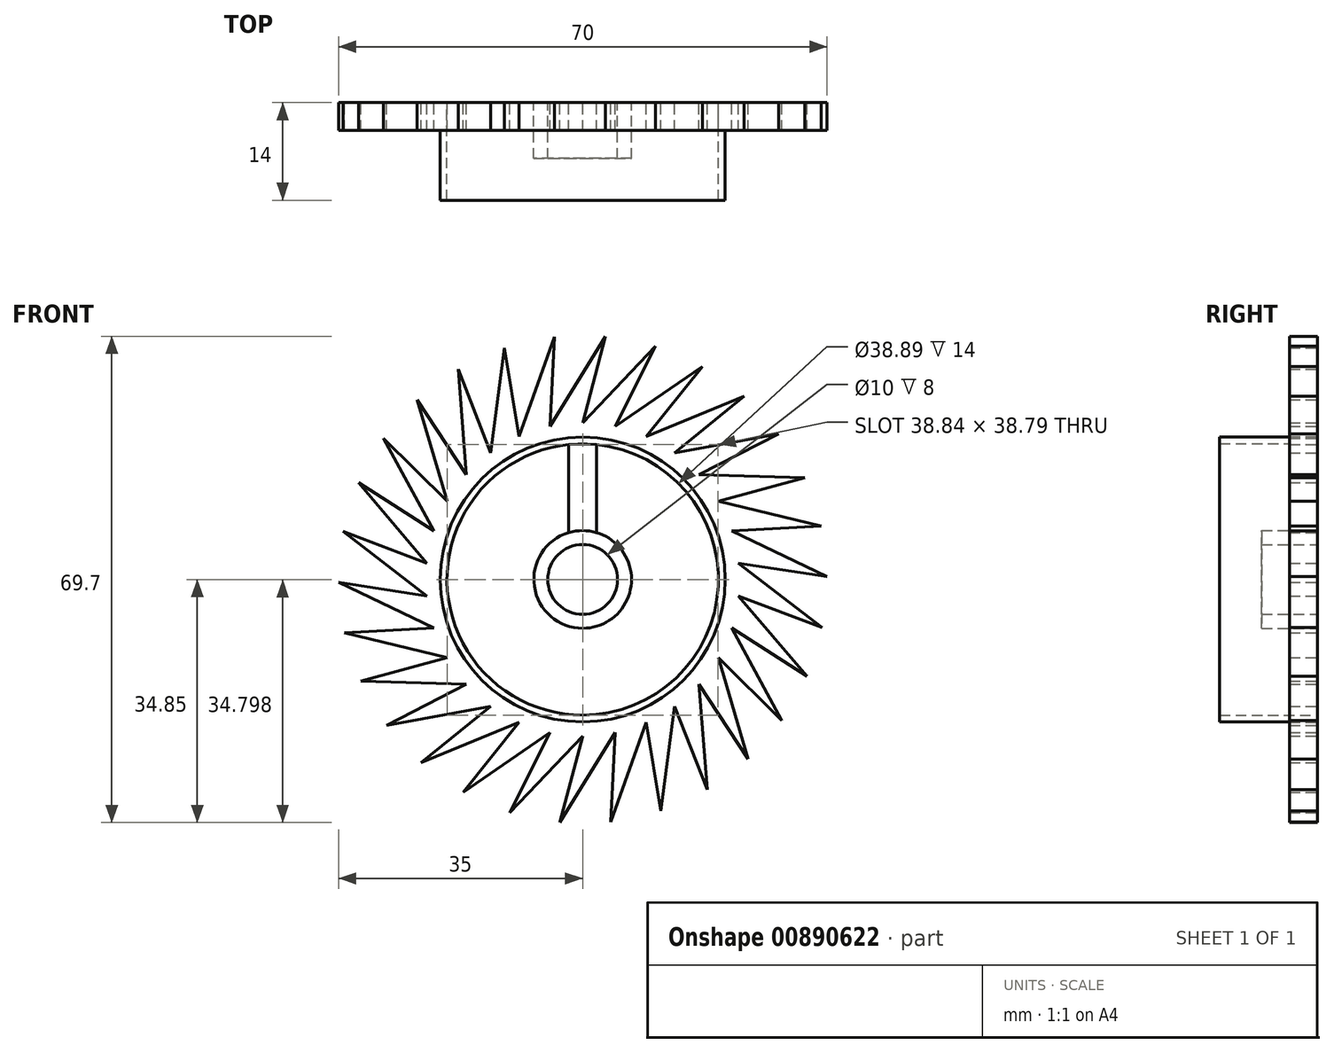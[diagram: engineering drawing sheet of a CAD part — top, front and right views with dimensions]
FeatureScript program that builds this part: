
annotation { "Feature Type Name" : "Feature", "Feature Type Description" : "" }
export const myFeature = defineFeature(function(context is Context, id is Id, definition is map)
    precondition{}
    {
        {
            var Q0;
            Q0=qCreatedBy(makeId("Front.planeOp"),FACE);
            var sketch = newSketch(context, id + "F0", { "sketchPlane" : qUnion([Q0])});
            skLineSegment(sketch, "E0", {"start": v(0, 0) * mm, "end": v(0, 22.44) * mm, "construction": true});
            skLineSegment(sketch, "E1", {"start": v(0, 0) * mm, "end": v(4.67, 21.95) * mm, "construction": true});
            skCircle(sketch, "E2", {"center": v(0, 0) * mm, "radius": 22.44 * mm, "construction": true});
            skLineSegment(sketch, "E3", {"start": v(0, 22.44) * mm, "end": v(10.44, 33.4) * mm});
            skLineSegment(sketch, "E4", {"start": v(10.44, 33.4) * mm, "end": v(4.67, 21.95) * mm});
            skCircle(sketch, "E5", {"center": v(0, 0) * mm, "radius": 35 * mm, "construction": true});
            skCircle(sketch, "E6", {"center": v(0, 0) * mm, "radius": 19.44 * mm});
            skLineSegment(sketch, "E7.1.0", {"start": v(-4.67, 21.95) * mm, "end": v(3.27, 34.85) * mm});
            skLineSegment(sketch, "E7.1.1", {"start": v(3.27, 34.85) * mm, "end": v(0, 22.44) * mm});
            skLineSegment(sketch, "E7.2.0", {"start": v(-9.13, 20.5) * mm, "end": v(-4.05, 34.76) * mm});
            skLineSegment(sketch, "E7.2.1", {"start": v(-4.05, 34.76) * mm, "end": v(-4.67, 21.95) * mm});
            skLineSegment(sketch, "E7.3.0", {"start": v(-13.2, 18.16) * mm, "end": v(-11.2, 33.16) * mm});
            skLineSegment(sketch, "E7.3.1", {"start": v(-11.2, 33.16) * mm, "end": v(-9.13, 20.5) * mm});
            skLineSegment(sketch, "E7.4.0", {"start": v(-16.68, 15.02) * mm, "end": v(-17.84, 30.11) * mm});
            skLineSegment(sketch, "E7.4.1", {"start": v(-17.84, 30.11) * mm, "end": v(-13.2, 18.16) * mm});
            skLineSegment(sketch, "E7.5.0", {"start": v(-19.44, 11.22) * mm, "end": v(-23.71, 25.74) * mm});
            skLineSegment(sketch, "E7.5.1", {"start": v(-23.71, 25.74) * mm, "end": v(-16.68, 15.02) * mm});
            skLineSegment(sketch, "E7.6.0", {"start": v(-21.35, 6.94) * mm, "end": v(-28.55, 20.25) * mm});
            skLineSegment(sketch, "E7.6.1", {"start": v(-28.55, 20.25) * mm, "end": v(-19.44, 11.22) * mm});
            skLineSegment(sketch, "E7.7.0", {"start": v(-22.32, 2.35) * mm, "end": v(-32.13, 13.87) * mm});
            skLineSegment(sketch, "E7.7.1", {"start": v(-32.13, 13.87) * mm, "end": v(-21.35, 6.94) * mm});
            skLineSegment(sketch, "E7.8.0", {"start": v(-22.32, -2.35) * mm, "end": v(-34.32, 6.89) * mm});
            skLineSegment(sketch, "E7.8.1", {"start": v(-34.32, 6.89) * mm, "end": v(-22.32, 2.35) * mm});
            skLineSegment(sketch, "E7.9.0", {"start": v(-21.35, -6.94) * mm, "end": v(-35, -0.4) * mm});
            skLineSegment(sketch, "E7.9.1", {"start": v(-35, -0.4) * mm, "end": v(-22.32, -2.35) * mm});
            skLineSegment(sketch, "E7.10.0", {"start": v(-19.44, -11.22) * mm, "end": v(-34.15, -7.66) * mm});
            skLineSegment(sketch, "E7.10.1", {"start": v(-34.15, -7.66) * mm, "end": v(-21.35, -6.94) * mm});
            skLineSegment(sketch, "E7.11.0", {"start": v(-16.68, -15.02) * mm, "end": v(-31.81, -14.6) * mm});
            skLineSegment(sketch, "E7.11.1", {"start": v(-31.81, -14.6) * mm, "end": v(-19.44, -11.22) * mm});
            skLineSegment(sketch, "E7.12.0", {"start": v(-13.2, -18.16) * mm, "end": v(-28.08, -20.9) * mm});
            skLineSegment(sketch, "E7.12.1", {"start": v(-28.08, -20.9) * mm, "end": v(-16.68, -15.02) * mm});
            skLineSegment(sketch, "E7.13.0", {"start": v(-9.13, -20.5) * mm, "end": v(-23.12, -26.27) * mm});
            skLineSegment(sketch, "E7.13.1", {"start": v(-23.12, -26.27) * mm, "end": v(-13.2, -18.16) * mm});
            skLineSegment(sketch, "E7.14.0", {"start": v(-4.67, -21.95) * mm, "end": v(-17.16, -30.5) * mm});
            skLineSegment(sketch, "E7.14.1", {"start": v(-17.16, -30.5) * mm, "end": v(-9.13, -20.5) * mm});
            skLineSegment(sketch, "E7.15.0", {"start": v(0, -22.44) * mm, "end": v(-10.44, -33.4) * mm});
            skLineSegment(sketch, "E7.15.1", {"start": v(-10.44, -33.4) * mm, "end": v(-4.67, -21.95) * mm});
            skLineSegment(sketch, "E7.16.0", {"start": v(4.67, -21.95) * mm, "end": v(-3.27, -34.85) * mm});
            skLineSegment(sketch, "E7.16.1", {"start": v(-3.27, -34.85) * mm, "end": v(0, -22.44) * mm});
            skLineSegment(sketch, "E7.17.0", {"start": v(9.13, -20.5) * mm, "end": v(4.05, -34.76) * mm});
            skLineSegment(sketch, "E7.17.1", {"start": v(4.05, -34.76) * mm, "end": v(4.67, -21.95) * mm});
            skLineSegment(sketch, "E7.18.0", {"start": v(13.2, -18.16) * mm, "end": v(11.2, -33.16) * mm});
            skLineSegment(sketch, "E7.18.1", {"start": v(11.2, -33.16) * mm, "end": v(9.13, -20.5) * mm});
            skLineSegment(sketch, "E7.19.0", {"start": v(16.68, -15.02) * mm, "end": v(17.84, -30.11) * mm});
            skLineSegment(sketch, "E7.19.1", {"start": v(17.84, -30.11) * mm, "end": v(13.2, -18.16) * mm});
            skLineSegment(sketch, "E7.20.0", {"start": v(19.44, -11.22) * mm, "end": v(23.71, -25.74) * mm});
            skLineSegment(sketch, "E7.20.1", {"start": v(23.71, -25.74) * mm, "end": v(16.68, -15.02) * mm});
            skLineSegment(sketch, "E7.21.0", {"start": v(21.35, -6.94) * mm, "end": v(28.55, -20.25) * mm});
            skLineSegment(sketch, "E7.21.1", {"start": v(28.55, -20.25) * mm, "end": v(19.44, -11.22) * mm});
            skLineSegment(sketch, "E7.22.0", {"start": v(22.32, -2.35) * mm, "end": v(32.13, -13.87) * mm});
            skLineSegment(sketch, "E7.22.1", {"start": v(32.13, -13.87) * mm, "end": v(21.35, -6.94) * mm});
            skLineSegment(sketch, "E7.23.0", {"start": v(22.32, 2.35) * mm, "end": v(34.32, -6.89) * mm});
            skLineSegment(sketch, "E7.23.1", {"start": v(34.32, -6.89) * mm, "end": v(22.32, -2.35) * mm});
            skLineSegment(sketch, "E7.24.0", {"start": v(21.35, 6.94) * mm, "end": v(35, 0.4) * mm});
            skLineSegment(sketch, "E7.24.1", {"start": v(35, 0.4) * mm, "end": v(22.32, 2.35) * mm});
            skLineSegment(sketch, "E7.25.0", {"start": v(19.44, 11.22) * mm, "end": v(34.15, 7.66) * mm});
            skLineSegment(sketch, "E7.25.1", {"start": v(34.15, 7.66) * mm, "end": v(21.35, 6.94) * mm});
            skLineSegment(sketch, "E7.26.0", {"start": v(16.68, 15.02) * mm, "end": v(31.81, 14.6) * mm});
            skLineSegment(sketch, "E7.26.1", {"start": v(31.81, 14.6) * mm, "end": v(19.44, 11.22) * mm});
            skLineSegment(sketch, "E7.27.0", {"start": v(13.2, 18.16) * mm, "end": v(28.08, 20.9) * mm});
            skLineSegment(sketch, "E7.27.1", {"start": v(28.08, 20.9) * mm, "end": v(16.68, 15.02) * mm});
            skLineSegment(sketch, "E7.28.0", {"start": v(9.13, 20.5) * mm, "end": v(23.12, 26.27) * mm});
            skLineSegment(sketch, "E7.28.1", {"start": v(23.12, 26.27) * mm, "end": v(13.2, 18.16) * mm});
            skLineSegment(sketch, "E7.29.0", {"start": v(4.67, 21.95) * mm, "end": v(17.16, 30.5) * mm});
            skLineSegment(sketch, "E7.29.1", {"start": v(17.16, 30.5) * mm, "end": v(9.13, 20.5) * mm});
            skCircle(sketch, "E8", {"center": v(0, 0) * mm, "radius": 1.5 * mm});
            skCircle(sketch, "E9", {"center": v(0, 0) * mm, "radius": 5 * mm});
            skLineSegment(sketch, "E10.top", {"start": v(-2, 22.36) * mm, "end": v(2, 22.36) * mm});
            skLineSegment(sketch, "E10.left", {"start": v(-2, 6.7) * mm, "end": v(-2, 22.36) * mm});
            skLineSegment(sketch, "E10.right", {"start": v(2, 6.7) * mm, "end": v(2, 22.36) * mm});
            skPoint(sketch, "E10.middle", {"position": v(0, 14.53) * mm});
            skCircle(sketch, "E11", {"center": v(0, 0) * mm, "radius": 7 * mm});
            skCircle(sketch, "E12", {"center": v(0, 0) * mm, "radius": 20.41 * mm});
            skSolve(sketch);
        }
        {
            var Q0;
            Q0=qCreatedBy(makeId("Top.planeOp"),FACE);
            var sketch = newSketch(context, id + "F1", { "sketchPlane" : qUnion([Q0])});
            skLineSegment(sketch, "E13", {"start": v(0, 0) * mm, "end": v(0, -18.3) * mm, "construction": true});
            skSolve(sketch);
        }
        {
            var Q0;
            Q0=makeQuery(id+"F0.imprint","IMPRINT",FACE,{"disambiguationData":[TD([[makeQuery(id+"F0.imprint","IMPRINT",EDGE,{"derivedFrom":sQuery(id+"F0.wireOp",EDGE,"E3")}),-1.0]])]});
            var Q1;
            {var subQ0=sQuery(id+"F0.wireOp",EDGE,"E10.top");Q1=makeQuery(id+"F0.imprint","IMPRINT",FACE,{"disambiguationData":[TD([[makeQuery(id+"F0.imprint","IMPRINT",EDGE,{"derivedFrom":subQ0}),-1.0]])]});}
            var Q2;
            {var subQ0=sQuery(id+"F0.wireOp",EDGE,"E10.left");var subQ1=sQuery(id+"F0.wireOp",EDGE,"E6");var subQ2=makeQuery(id+"F0.imprint","INTERSECT",VERTEX,{"derivedFrom":[subQ1,subQ0]});Q2=makeQuery(id+"F0.imprint","IMPRINT",FACE,{"disambiguationData":[TD([[makeQuery(id+"F0.imprint","IMPRINT",EDGE,{"disambiguationData":[TD([[subQ2,-1.0]])],"derivedFrom":subQ1}),-1.0]])]});}
            extrude(context, id + "F2", {"entities" : qUnion([Q0, Q1, Q2]), "depth" : 4 * mm, "offsetDistance" : 25 * mm});
        }
        {
            var Q0;
            {var subQ0=sQuery(id+"F0.wireOp",EDGE,"E10.left");var subQ1=sQuery(id+"F0.wireOp",EDGE,"E6");var subQ2=makeQuery(id+"F0.imprint","INTERSECT",VERTEX,{"derivedFrom":[subQ1,subQ0]});Q0=makeQuery(id+"F0.imprint","IMPRINT",FACE,{"disambiguationData":[TD([[makeQuery(id+"F0.imprint","IMPRINT",EDGE,{"disambiguationData":[TD([[subQ2,-1.0]])],"derivedFrom":subQ1}),-1.0]])]});}
            var Q1;
            {var subQ0=sQuery(id+"F0.wireOp",EDGE,"E10.left");var subQ1=sQuery(id+"F0.wireOp",EDGE,"E6");var subQ2=makeQuery(id+"F0.imprint","INTERSECT",VERTEX,{"derivedFrom":[subQ1,subQ0]});Q1=makeQuery(id+"F0.imprint","IMPRINT",FACE,{"disambiguationData":[TD([[makeQuery(id+"F0.imprint","IMPRINT",EDGE,{"disambiguationData":[TD([[subQ2,1.0]])],"derivedFrom":subQ1}),-1.0]])]});}
            extrude(context, id + "F3", {"entities" : qUnion([Q0, Q1]), "operationType" : NewBodyOperationType.ADD, "depth" : 14 * mm, "offsetDistance" : 25 * mm});
        }
        {
            var Q0;
            Q0=makeQuery(id+"F0.imprint","IMPRINT",FACE,{"disambiguationData":[TD([[makeQuery(id+"F0.imprint","IMPRINT",EDGE,{"derivedFrom":sQuery(id+"F0.wireOp",EDGE,"E9")}),-1.0]])]});
            extrude(context, id + "F4", {"entities" : qUnion([Q0]), "depth" : 8 * mm, "offsetDistance" : 25 * mm});
        }
        {
            var Q0;
            {var subQ0=sQuery(id+"F0.wireOp",EDGE,"E10.left");var subQ1=sQuery(id+"F0.wireOp",EDGE,"E6");var subQ2=makeQuery(id+"F0.imprint","INTERSECT",VERTEX,{"derivedFrom":[subQ1,subQ0]});Q0=makeQuery(id+"F0.imprint","IMPRINT",FACE,{"disambiguationData":[TD([[makeQuery(id+"F0.imprint","IMPRINT",EDGE,{"disambiguationData":[TD([[subQ2,1.0]])],"derivedFrom":subQ1}),1.0]])]});}
            extrude(context, id + "F5", {"entities" : qUnion([Q0]), "operationType" : NewBodyOperationType.ADD, "depth" : 4 * mm, "offsetDistance" : 25 * mm});
        }
    });
